# Revit family: Lighting Fixture_Sylvania_Expospot 90 Cardan Trio_Ceiling Recessed1
name_source: partatom
category: Lighting Fixtures
revit_build: Autodesk Revit 2016 (Build: 20161004_0715(x64)
units: mm (PartAtom-declared; Revit-internal decimal feet)

## family parameters
Cut with Voids When Loaded = No
Host = Face
Light Source = No
OmniClass Number = 23.80.70.11.17
OmniClass Title = Specialized Lighting by Location or Use
Part Type = Normal
Room Calculation Point = No
Round Connector Dimension = Use Diameter
Shared = No

## types (24) — shared parameters
Assembly Code = D5020200
Average Life = 50 000h
Body Material = Aluminum_Sylvania_Expospot_White
Body Secondary Material = Plastic_Sylvania_Expospot_Black
Body Void Radius = 58 mm
Colour Variation Initial = 3SDCM
Control Gear Mounting = Remote
Control Gear Required = No
Control Gear Type = Electronic
Description = Specifically designed for Retail and Display applications. I.e. Supermarkets Fashion Retail Department stores. Build around a 90mm reflector and lens combination.
Dimmable = N
Drive Current = 700mA
Electrical Protection = Class II
Glow Wire Test = 850 °C
Head Center Offset = 88.5 mm  [stored 0.290354 ft]
Head Diameter = 100 mm  [stored 0.328084 ft]
Head Radius = 50 mm  [stored 0.164042 ft]
Height = 104 mm
IK Rating = IK02
IP Rating = IP20
Inrush Current = 58 A
Inrush Duration = 250µs
LOR = 100%
Lamp = LED
Length = 437 mm  [stored 1.43373 ft]
Light Loss Factor = 1
Manufacturer = Feilo Sylvania
Max. Luminaires per 10A B Breaker = 4
Max. Luminaires per 10A C Breaker = 7
Max. Luminaires per 13A B Breaker = 6
Max. Luminaires per 13A C Breaker = 9
Max. Luminaires per 16A B Breaker = 7
Max. Luminaires per 16A C Breaker = 11
Max. Luminaires per 20A B Breaker = 9
Max. Luminaires per 20A C Breaker = 15
Mounting Width Inner = 55 mm  [stored 0.180446 ft]
Mounting Width Outer = 63 mm  [stored 0.206693 ft]
Nominal Frequency = 50/60Hz
Photobiological Risk Group = RG1
Product Family = EXPOSPOT 90 CARDAN
Product Page URL = http://www.sylvania-lighting.com
Reflector Material = Aluminum_Sylvania_Expospot_Polished
URL = http://www.sylvania-lighting.com
Voltage = 240 V
Voltage Comments = 220-240V~
Weight = 3 kg
Width = 163 mm  [stored 0.534777 ft]
zero-valued in all types: Default Elevation

## per-type parameters (varying)
| type | Apparent Load | Apparent Load Per Head | Beam Angle | CRI | Diffuser Material | Initial Color | Initial Intensity | Initial Intensity Per Head | Lamp Power Factor | Photometric Web File | Product Code | Total Power Consumption | Total Power Consumption Per Head |
| EXPOSPOT 90 TRIO HO 90 4K W WH | 107 VA | 35 VA | 57° | 90Ra | Acrylic_Sylvania_Expospot_4000K | 4000 K | 3 x 3479lm | 3479 lm | 0.95 | IES_Expospot_90_Cardan_Trio : 0060392 | 0060392 | 107 W | 35 W |
| EXPOSPOT 90 TRIO HO 90 4K M WH | 107 VA | 35 VA | 43° | 90Ra | Acrylic_Sylvania_Expospot_4000K | 4000 K | 3 x 3458lm | 3458 lm | 0.95 | IES_Expospot_90_Cardan_Trio : 0060391 | 0060391 | 107 W | 35 W |
| EXPOSPOT 90 TRIO HO 90 4K N WH | 107 VA | 35 VA | 26° | 90Ra | Acrylic_Sylvania_Expospot_4000K | 4000 K | 3 x 3570lm | 3570 lm | 0.95 | IES_Expospot_90_Cardan_Trio : 0060390 | 0060390 | 107 W | 35 W |
| EXPOSPOT 90 TRIO HO 90 3K W WH | 107 VA | 35 VA | 56° | 90Ra | Acrylic_Sylvania_Expospot_3000K | 3000 K | 3 x 3293lm | 3293 lm | 0.95 | IES_Expospot_90_Cardan_Trio : 0060380 | 0060380 | 107 W | 35 W |
| EXPOSPOT 90 TRIO HO 90 3K M WH | 107 VA | 35 VA | 44° | 90Ra | Acrylic_Sylvania_Expospot_3000K | 3000 K | 3 x 3180lm | 3180 lm | 0.95 | IES_Expospot_90_Cardan_Trio : 0060379 | 0060379 | 107 W | 35 W |
| EXPOSPOT 90 TRIO HO 90 3K N WH | 107 VA | 35 VA | 26° | 90Ra | Acrylic_Sylvania_Expospot_3000K | 3000 K | 3 x 3369lm | 3369 lm | 0.95 | IES_Expospot_90_Cardan_Trio : 0060378 | 0060378 | 107 W | 35 W |
| EXPOSPOT 90 TRIO HO 80 4K W WH | 107 VA | 35 VA | 57° | 80Ra | Acrylic_Sylvania_Expospot_4000K | 4000 K | 3 x 3942lm | 3942 lm | 0.95 | IES_Expospot_90_Cardan_Trio : 0060368 | 0060368 | 107 W | 35 W |
| EXPOSPOT 90 TRIO HO 80 4K M WH | 107 VA | 35 VA | 43° | 80Ra | Acrylic_Sylvania_Expospot_4000K | 4000 K | 3 x 3852lm | 3852 lm | 0.95 | IES_Expospot_90_Cardan_Trio : 0060367 | 0060367 | 107 W | 35 W |
| EXPOSPOT 90 TRIO HO 80 4K N WH | 107 VA | 35 VA | 26° | 80Ra | Acrylic_Sylvania_Expospot_4000K | 4000 K | 3 x 4121lm | 4121 lm | 0.95 | IES_Expospot_90_Cardan_Trio : 0060366 | 0060366 | 107 W | 35 W |
| EXPOSPOT 90 TRIO HO 80 3K W WH | 107 VA | 35 VA | 56° | 80Ra | Acrylic_Sylvania_Expospot_3000K | 3000 K | 3 x 3736lm | 3736 lm | 0.95 | IES_Expospot_90_Cardan_Trio : 0060356 | 0060356 | 107 W | 35 W |
| EXPOSPOT 90 TRIO HO 80 3K M WH | 107 VA | 35 VA | 44° | 80Ra | Acrylic_Sylvania_Expospot_3000K | 3000 K | 3 x 3721lm | 3721 lm | 0.95 | IES_Expospot_90_Cardan_Trio : 0060355 | 0060355 | 107 W | 35 W |
| EXPOSPOT 90 TRIO HO 80 3K N WH | 107 VA | 35 VA | 26° | 80Ra | Acrylic_Sylvania_Expospot_3000K | 3000 K | 3 x 3946lm | 3946 lm | 0.95 | IES_Expospot_90_Cardan_Trio : 0060354 | 0060354 | 107 W | 35 W |
| EXPOSPOT 90 TRIO HE 90 4K W WH | 77 VA | 28 VA | 57° | 90Ra | Acrylic_Sylvania_Expospot_4000K | 4000 K | 3 x 2855lm | 2855 lm | 0.92 | IES_Expospot_90_Cardan_Trio : 0060344 | 0060344 | 77 W | 28 W |
| EXPOSPOT 90 TRIO HE 90 4K M WH | 77 VA | 28 VA | 45° | 90Ra | Acrylic_Sylvania_Expospot_4000K | 4000 K | 3 x 2836lm | 2836 lm | 0.92 | IES_Expospot_90_Cardan_Trio : 0060343 | 0060343 | 77 W | 28 W |
| EXPOSPOT 90 TRIO HE 90 4K N WH | 77 VA | 28 VA | 26° | 90Ra | Acrylic_Sylvania_Expospot_4000K | 4000 K | 3 x 2789lm | 2789 lm | 0.92 | IES_Expospot_90_Cardan_Trio : 0060342 | 0060342 | 77 W | 28 W |
| EXPOSPOT 90 TRIO HE 90 3K W WH | 77 VA | 28 VA | 58° | 90Ra | Acrylic_Sylvania_Expospot_3000K | 3000 K | 3 x 2589lm | 2589 lm | 0.92 | IES_Expospot_90_Cardan_Trio : 0060332 | 0060332 | 77 W | 28 W |
| EXPOSPOT 90 TRIO HE 90 3K M WH | 77 VA | 28 VA | 44° | 90Ra | Acrylic_Sylvania_Expospot_3000K | 3000 K | 3 x 2573lm | 2573 lm | 0.92 | IES_Expospot_90_Cardan_Trio : 0060331 | 0060331 | 77 W | 28 W |
| EXPOSPOT 90 TRIO HE 90 3K N WH | 77 VA | 28 VA | 25° | 90Ra | Acrylic_Sylvania_Expospot_3000K | 3000 K | 3 x 2536lm | 2536 lm | 0.92 | IES_Expospot_90_Cardan_Trio : 0060330 | 0060330 | 77 W | 28 W |
| EXPOSPOT 90 TRIO HE 80 4K W WH | 77 VA | 28 VA | 57° | 80Ra | Acrylic_Sylvania_Expospot_4000K | 4000 K | 3 x 3229lm | 3229 lm | 0.92 | IES_Expospot_90_Cardan_Trio : 0060320 | 0060320 | 77 W | 28 W |
| EXPOSPOT 90 TRIO HE 80 4K M WH | 77 VA | 28 VA | 43° | 80Ra | Acrylic_Sylvania_Expospot_4000K | 4000 K | 3 x 3232lm | 3232 lm | 0.92 | IES_Expospot_90_Cardan_Trio : 0060319 | 0060319 | 77 W | 28 W |
| EXPOSPOT 90 TRIO HE 80 4K N WH | 77 VA | 28 VA | 29° | 80Ra | Acrylic_Sylvania_Expospot_4000K | 4000 K | 3 x 3145lm | 3145 lm | 0.92 | IES_Expospot_90_Cardan_Trio : 0060318 | 0060318 | 77 W | 28 W |
| EXPOSPOT 90 TRIO HE 80 3K W WH | 77 VA | 28 VA | 61° | 80Ra | Acrylic_Sylvania_Expospot_3000K | 3000 K | 3 x 3174lm | 3174 lm | 0.92 | IES_Expospot_90_Cardan_Trio : 0060308 | 0060308 | 77 W | 28 W |
| EXPOSPOT 90 TRIO HE 80 3K M WH | 77 VA | 28 VA | 47° | 80Ra | Acrylic_Sylvania_Expospot_3000K | 3000 K | 3 x 3126lm | 3126 lm | 0.92 | IES_Expospot_90_Cardan_Trio : 0060307 | 0060307 | 77 W | 28 W |
| EXPOSPOT 90 TRIO HE 80 3K N WH | 77 VA | 28 VA | 26° | 80Ra | Acrylic_Sylvania_Expospot_3000K | 3000 K | 3 x 3174lm | 3174 lm | 0.92 | IES_Expospot_90_Cardan_Trio : 0060306 | 0060306 | 77 W | 28 W |

note: column(s) folded — value = type name in every type: Model

note: [stored X ft] marks values corroborated as IEEE doubles in the binary element streams (Revit-internal decimal feet)

## geometry (parser evidence)
native form markers: Sweep x6
no freeform markers — native parametric forms only
